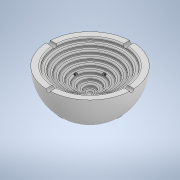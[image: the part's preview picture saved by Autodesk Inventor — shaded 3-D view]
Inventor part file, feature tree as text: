
AUTODESK INVENTOR PART (.ipt)
format: ipt  version: 2022 (Build 260153000, 153)  size: 511,488 bytes
history: native  units: mm
features: extrude x16, sketch x16, other x9, fillet x5
ambient origin geometry x8: Origin, YZ Plane, XZ Plane, XY Plane, X Axis, Y Axis, Z Axis, Center Point
bodies: Body1 (feature_tree)
feature tree (46):
  other  "實體1"
  extrude  "擠出1"  Depth=60.0mm
  fillet  "圓角1"  Radius=30.0mm
  extrude  "擠出2"  Depth=30.0mm
  extrude  "擠出3"  Depth=50.0mm
  extrude  "擠出4"  Depth=2.0mm TaperAngle=0.0deg
  extrude  "擠出5"  Depth=44.0mm
  extrude  "擠出6"  Depth=2.0mm TaperAngle=0.0deg
  extrude  "擠出7"  Depth=38.0mm
  extrude  "擠出8"  Depth=2.0mm TaperAngle=0.0deg
  extrude  "擠出9"  Depth=32.0mm
  extrude  "擠出11"  Depth=2.0mm TaperAngle=0.0deg
  extrude  "擠出12"  Depth=26.0mm
  extrude  "擠出13"  Depth=2.0mm TaperAngle=0.0deg
  extrude  "擠出16"  Depth=20.0mm
  fillet  "圓角2"  Radius=2.0mm
  extrude  "擠出17"  Depth=14.0mm
  fillet  "圓角3"  Radius=2.0mm
  extrude  "擠出18"  Depth=8.0mm
  fillet  "圓角4"  Radius=2.0mm
  extrude  "擠出19"  Depth=3.0mm
  fillet  "圓角5"  Radius=20.0mm
  other  "面圓角1"
  other  "面圓角2"
  other  "面圓角3"
  other  "面圓角4"
  other  "面圓角5"
  other  "面圓角6"
  other  "面圓角7"
  other  "面圓角8"
  sketch  "草圖3"
  sketch  "草圖4"
  sketch  "草圖5"
  sketch  "草圖6"
  sketch  "草圖7"
  sketch  "草圖8"
  sketch  "草圖9"
  sketch  "草圖10"
  sketch  "草圖11"
  sketch  "草圖14"
  sketch  "草圖15"
  sketch  "草圖16"
  sketch  "草圖25"
  sketch  "草圖26"
  sketch  "草圖27"
  sketch  "草圖29"
